# Revit family: Resideo_GasAlarm_R200xxx
name_source: partatom
category: Specialty Equipment
units: mm (PartAtom-declared; Revit-internal decimal feet)

## family parameters
Cut with Voids When Loaded = No
Host = Face
OmniClass Number = 23.80.50.00
OmniClass Title = Terminals for Power Supply
Part Type = Normal
Room Calculation Point = No
Round Connector Dimension = Use Diameter
Shared = No

## types (6) — shared parameters
Assembly Code = D5030700
AssetType = Fixed
BIMObjectName = Resideo_GasAlarm_R200
BatteryLife = 10 years
Button = Test/Silence
ClassificationName = Uniclass2015
ClassificationValue = Pr_75_80_30_82
DocumentationInstallationGuide = https://www.bimstore.co
DocumentationLiterature1 = https://www.bimstore.co
DocumentationLiterature2 = https://www.bimstore.co
DocumentationLiterature3 = https://www.bimstore.co
DocumentationMaintenance = https://www.bimstore.co
DurationUnit = Year
IfcExportAs = IfcSensorType
IfcExportType = USERDEFINED
InstallationType = Wall, Ceiling
Keynote = W
Languages = Dutch, English, French, German, Italian, Portuguese, Spanish, Swedish
Manufacturer = Resideo
ManufacturerName = Resideo
NBSDescription = Smoke and heat multi-sensor detectors
NBSObjectName = Resideo - Smoke and heat multi-sensor detectors
NBSReference = 90-75-30/331
PowerSupply = Battery, 3VDC
PrimaryMaterial = Resideo - Plastic - White
ProductionYear = 2022
ScopeOfSupply = Package and manual
SecondaryMaterial = Resideo - Plastic - Black
URL = https://www.resideo.com
WarrantyDurationLabor = 0
WarrantyDurationParts = 10
WarrantyDurationUnit = Year
WarrantyGuarantorLabor = https://www.resideo.com
WarrantyGuarantorParts = https://www.resideo.com
_BSBibleVersion = 16
_CurrentRevision = 1
_DistributedBy = https://www.bimstore.co
_ObjectUserGuide = https://www.bimstore.co
zero-valued in all types: Cost, Default Elevation, ExpectedLife, _BimSpecGuid

## per-type parameters (varying)
- R200C-1: 1=Yes; 2=No; 3=No; 4=No; Audible=>85dB @3m; Battery=CR17450; Description=Carbon Monoxide (CO) Alarm Western Europe; DetectionPrinciple=Electrochemical Cell; GasDetected=Carbon Monoxide; Humidity=25% - 95% RH; IPRating=IP44; ModelReference=Carbon Monoxide (CO) Alarm Western Europe; NominalDepth=95 mm; NominalHeight=25 mm  [stored 0.082021 ft]; NominalLength=95 mm; ReferencedStandard=EN 62368-1:2014 | EN IEC 63000:2018 | EN 50270:2015 | EN 50291 | NF, Kitemark, B-Mark; Size=95mm (D) x 25mm (H) x 95mm (L); Temperature=-10˚C / +40˚C; ThirdPartyApprovals=EN 62368-1:2014 | EN IEC 63000:2018 | EN 50270:2015 | EN 50291 | NF, Kitemark, B-Mark; Type Comments=Carbon Monoxide (CO) Alarm Western Europe; VisualIndicator=Big text: ALARM, flashing in red; Weight=0.12 kg
- R200C-N1: 1=Yes; 2=No; 3=No; 4=No; Audible=>85dB @3m; Battery=CR17450; Description=Interconnected Carbon Monoxide (CO) Alarm Western Europe; DetectionPrinciple=Electrochemical Cell; GasDetected=Carbon Monoxide; Humidity=25% - 95% RH; IPRating=IP44; Interconnections=Yes (Maximum 12 alarms); ModelReference=Interconnected Carbon Monoxide (CO) Alarm Western Europe; NominalDepth=95 mm; NominalHeight=25 mm  [stored 0.082021 ft]; NominalLength=95 mm; RFDistance=100 metres; RFFrequency=868 Mhz; ReferencedStandard=EN 62368-1:2014 | EN IEC 63000:2018 | EN 50270:2015 | EN 50291 | NF, Kitemark, B-Mark; Size=95mm (D) x 25mm (H) x 95mm (L); Temperature=-10˚C / +45˚C; ThirdPartyApprovals=EN 62368-1:2014 | EN IEC 63000:2018 | EN 50270:2015 | EN 50291 | NF, Kitemark, B-Mark; Type Comments=Interconnected Carbon Monoxide (CO) Alarm Western Europe; VisualIndicator=Big text: ALARM, flashing in red; Weight=0.12 kg
- R200S-1: 1=No; 2=Yes; 3=No; 4=No; Audible=85dB @3m; Battery=CR123A; Description=Smoke Alarm Western Europe; DetectionPrinciple=Optical Sensor; GasDetected=Smoke; Humidity=25% - 93% RH; IPRating=IP20; ModelReference=Smoke Alarm Western Europe; NominalDepth=116 mm; NominalHeight=23 mm; NominalLength=116 mm; ReferencedStandard=CE | Q label | NF | SBSC | VdS | EN 14604:2005 + AC:2008 | UKCA | EN 62368-1:2014 | Kitemark | BS 5446-2:2003; Size=116mm (D) x 24mm (H) x 116mm (L); Temperature=0˚C / +40˚C; ThirdPartyApprovals=CE | Q label | NF | SBSC | VdS | EN 14604:2005 + AC:2008 | UKCA | EN 62368-1:2014 | Kitemark | BS 5446-2:2003; Type Comments=Smoke Alarm Western Europe; VisualIndicator=Flashing red LED; Weight=0.12 kg
- R200S-N1: 1=No; 2=No; 3=Yes; 4=No; Audible=85dB @3m; Battery=CR17450; Description=Interconnected Smoke Alarm Western Europe; DetectionPrinciple=Optical Sensor; GasDetected=Smoke; Humidity=25% - 93% RH; IPRating=IP20; Interconnections=Yes (Maximum 12 alarms); ModelReference=Interconnected Smoke Alarm Western Europe; NominalDepth=104 mm; NominalHeight=41 mm; NominalLength=104 mm; RFDistance=100 metres; RFFrequency=868 Mhz; ReferencedStandard=CE | Q label | NF | SBSC | VdS | EN 14604:2005 + AC:2008 | UKCA | EN 62368-1:2014 | Kitemark | BS 5446-2:2003; Size=104mm (D) x 42mm (H) x 104mm (L); Temperature=0˚C / +40˚C; ThirdPartyApprovals=CE | Q label | NF | SBSC | VdS | EN 14604:2005 + AC:2008 | UKCA | EN 62368-1:2014 | Kitemark | BS 5446-2:2003; Type Comments=Interconnected Smoke Alarm Western Europe; VisualIndicator=Flashing red LED; Weight=0.15 kg
- R200H-N1: 1=No; 2=No; 3=No; 4=Yes; Audible=85dB @3m; Battery=CR17450; Description=Heat Alarm Western Europe; DetectionPrinciple=Thermal Sensor; GasDetected=Heat; Humidity=< 93%; IPRating=IP20; Interconnections=Yes (Maximum 12 alarms); ModelReference=Heat Alarm Western Europe; NominalDepth=104 mm; NominalHeight=55 mm; NominalLength=104 mm; RFDistance=100 metres; RFFrequency=868 Mhz; ReferencedStandard=CE | Q label | VdS | EN 14604:2005 + AC:2008 | UKCA | EN 62368-1:2014; Size=104mm (D) x 56mm (H) x 104mm (L); Temperature=4˚C / +50˚C; ThirdPartyApprovals=CE | Q label | VdS | EN 14604:2005 + AC:2008 | UKCA | EN 62368-1:2014; Type Comments=Heat Alarm Western Europe; VisualIndicator=Flashing red LED; Weight=0.15 kg
- R200ST-N1: 1=No; 2=No; 3=No; 4=Yes; Audible=85dB @3m; Battery=CR17450; Description=Interconnected Smoke+Heat Alarm Western Europe; DetectionPrinciple=Thermal Sensor; GasDetected=Heat and Smoke; Humidity=< 93%; IPRating=IP20; Interconnections=Yes (Maximum 12 alarms); ModelReference=Interconnected Smoke+Heat Alarm Western Europe; NominalDepth=104 mm; NominalHeight=55 mm; NominalLength=104 mm; RFDistance=100 metres; RFFrequency=868 Mhz; ReferencedStandard=CE | Q label | SBSC | VdS | EN 14604:2005 + AC:2008 | UKCA | EN 62368-1:2014; Size=104mm (D) x 56mm (H) x 104mm (L); Temperature=0˚C / +40˚C; ThirdPartyApprovals=CE | Q label | SBSC | VdS | EN 14604:2005 + AC:2008 | UKCA | EN 62368-1:2014; Type Comments=Interconnected Smoke+Heat Alarm Western Europe; VisualIndicator=Flashing red LED; Weight=0.16 kg

note: column(s) folded — value = type name in every type: Model, ModelNumber, TypeName

note: [stored X ft] marks values corroborated as IEEE doubles in the binary element streams (Revit-internal decimal feet)

## geometry (parser evidence)
native form markers: Sweep x3
no freeform markers — native parametric forms only
